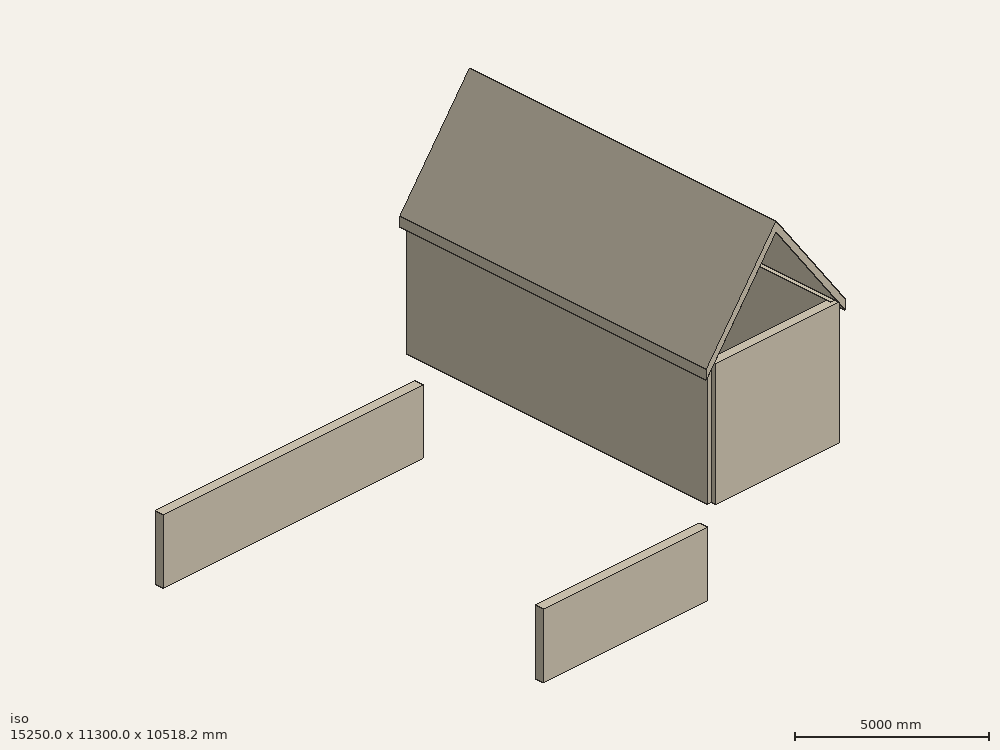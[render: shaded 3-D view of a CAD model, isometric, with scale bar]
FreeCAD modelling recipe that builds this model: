
FCSTD DOCUMENT  (FreeCAD 0.16R6706 (Git))
Label: HorseShoeLane
License: All rights reserved
LicenseURL: http://en.wikipedia.org/wiki/All_rights_reserved
objects: Part::Part2DObjectPython×12, Part::FeaturePython×10, App::DocumentObjectGroup×2, App::DocumentObjectGroupPython×2, Sketcher::SketchObject×1
note: 23 computed .brp shape members not serialized (recipe doc carries the construction recipe); baked Part::Feature solids carry a one-line shape summary decoded from their .brp

FEATURE [Part::Part2DObjectPython] Line  label="External North"  # Draft 2D object (typed FeaturePython)
  ChamferSize = 0
  Closed = false
  End = (4500,0,0)
  FilletRadius = 0
  Length = 4500
  MakeFace = true
  Points = (2) [(0,0,0),(4500,2.75546e-13,0)]
  Start = (0,0,0)
  Subdivisions = 0
FEATURE [Part::Part2DObjectPython] Line001  label="External West"  # Draft 2D object (typed FeaturePython)
  ChamferSize = 0
  Closed = false
  End = (0,-11000,0)
  FilletRadius = 0
  Length = 11000
  MakeFace = true
  Points = (2) [(0,0,0),(0,-11000,0)]
  Start = (0,0,0)
  Subdivisions = 0
FEATURE [Part::Part2DObjectPython] Line002  label="External East N"  # Draft 2D object (typed FeaturePython)
  ChamferSize = 0
  Closed = false
  End = (5600,-5600,0)
  FilletRadius = 0
  Length = 5600
  MakeFace = true
  Points = (2) [(5600,3.42901e-13,0),(5600,-5600,0)]
  Start = (5600,0,0)
  Subdivisions = 0
FEATURE [Part::Part2DObjectPython] Line003  label="External South"  # Draft 2D object (typed FeaturePython)
  ChamferSize = 0
  Closed = false
  End = (4500,-11000,0)
  FilletRadius = 0
  Length = 4500
  MakeFace = true
  Points = (2) [(0,-11000,0),(4500,-11000,0)]
  Start = (0,-11000,0)
  Subdivisions = 0
FEATURE [Part::Part2DObjectPython] Line004  label="External East S"  # Draft 2D object (typed FeaturePython)
  ChamferSize = 0
  Closed = false
  End = (4500,-5600,0)
  FilletRadius = 0
  Length = 5400
  MakeFace = true
  Points = (2) [(4500,-11000,0),(4500,-5600,0)]
  Start = (4500,-11000,0)
  Subdivisions = 0
FEATURE [Part::Part2DObjectPython] Line005  label="External Porch South"  # Draft 2D object (typed FeaturePython)
  ChamferSize = 0
  Closed = false
  End = (5600,-5600,0)
  FilletRadius = 0
  Length = 1100
  MakeFace = true
  Points = (2) [(4500,-5600,0),(5600,-5600,0)]
  Start = (4500,-5600,0)
  Subdivisions = 0
FEATURE [App::DocumentObjectGroup] Group  label="Main Cottage"
  Group = -> [Line,Line001,Line002,Line003,Line004,Line005]
FEATURE [Part::Part2DObjectPython] Line006  label="LF External North"  # Draft 2D object (typed FeaturePython)
  ChamferSize = 0
  Closed = false
  End = (-9500,-300,-3000)
  FilletRadius = 0
  Length = 9500
  MakeFace = true
  Placement = pos=(0,-300,-3000) rot=(0,0,1;0rad)
  Points = (2) [(0,0,0),(-9500,-5.81707e-13,0)]
  Start = (0,-300,-3000)
  Subdivisions = 0
FEATURE [Part::Part2DObjectPython] Line007  label="LF External South"  # Draft 2D object (typed FeaturePython)
  ChamferSize = 0
  Closed = false
  End = (-6000,-10700,-3000)
  FilletRadius = 0
  Length = 6000
  MakeFace = true
  Placement = pos=(0,300,-3000) rot=(0,0,1;0rad)
  Points = (2) [(0,-11000,0),(-6000,-11000,0)]
  Start = (0,-10700,-3000)
  Subdivisions = 0
FEATURE [App::DocumentObjectGroup] Group001  label="Lower Floor"
  Group = -> [Line006,Line007]
FEATURE [Part::FeaturePython] Wall  label="LF South Wall"  # WARN: FeaturePython — macro-defined, semantics opaque (R4)
  Align = 2
  Base = -> Line007
  Face = 0
  Height = 2200
  Length = 6000
  MoveWithHost = false
  Normal = (0,0,0)
  Role = 0
  Width = 300
FEATURE [Part::FeaturePython] Wall001  label="LF North Wall"  # WARN: FeaturePython — macro-defined, semantics opaque (R4)
  Align = 2
  Base = -> Line006
  Face = 0
  Height = 2200
  Length = 9500
  MoveWithHost = false
  Normal = (0,0,0)
  Role = 0
  Width = 300
FEATURE [App::DocumentObjectGroupPython] Floor  label="Lower Floor001"  # scripted group (container) (typed FeaturePython)
  Group = -> [Wall,Wall001]
  Height = 0
FEATURE [Part::Part2DObjectPython] Line008  label="External Porch North"  # Draft 2D object (typed FeaturePython)
  ChamferSize = 0
  Closed = false
  End = (5600,0,0)
  FilletRadius = 0
  Length = 1100
  MakeFace = true
  Placement = pos=(0,5600,0) rot=(0,0,1;0rad)
  Points = (2) [(4500,-5600,0),(5600,-5600,0)]
  Start = (4500,0,0)
  Subdivisions = 0
FEATURE [Part::Part2DObjectPython] Line009  label="MC Internal East"  # Draft 2D object (typed FeaturePython)
  ChamferSize = 0
  Closed = false
  End = (4500,0,0)
  FilletRadius = 0
  Length = 5600
  MakeFace = true
  Points = (2) [(4500,-5600,0),(4500,2.75546e-13,0)]
  Start = (4500,-5600,0)
  Subdivisions = 0
FEATURE [Sketcher::SketchObject] Sketch
  sketch-geometry (3):
    g0: LineSegment StartX=4500 StartY=0 StartZ=0 EndX=5600 EndY=0 EndZ=0
    g1: LineSegment StartX=4500 StartY=-5600 StartZ=0 EndX=5600 EndY=-5600 EndZ=0
    g2: LineSegment StartX=5600 StartY=0 StartZ=0 EndX=5600 EndY=-5600 EndZ=0
FEATURE [Part::FeaturePython] Wall008  label="MC Porch North Wall"  # WARN: FeaturePython — macro-defined, semantics opaque (R4)
  Align = 2
  Base = -> Sketch
  Face = 0
  Height = 2100
  Length = 7800
  MoveWithHost = false
  Normal = (0,0,0)
  Role = 0
  Width = 300
FEATURE [Part::FeaturePython] Wall003  label="MC South Wall"  # WARN: FeaturePython — macro-defined, semantics opaque (R4)
  Align = 2
  Base = -> Line003
  Face = 0
  Height = 4200
  Length = 4500
  MoveWithHost = false
  Normal = (0,0,0)
  Role = 0
  Width = 300
FEATURE [Part::FeaturePython] Wall004  label="MC External West Wall"  # WARN: FeaturePython — macro-defined, semantics opaque (R4)
  Align = 2
  Base = -> Line001
  Face = 0
  Height = 4200
  Length = 11000
  MoveWithHost = false
  Normal = (0,0,0)
  Role = 0
  Width = 300
FEATURE [Part::FeaturePython] Wall006  label="MC External East S Wall"  # WARN: FeaturePython — macro-defined, semantics opaque (R4)
  Align = 2
  Base = -> Line004
  Face = 0
  Height = 4200
  Length = 5400
  MoveWithHost = false
  Normal = (0,0,0)
  Role = 0
  Width = 300
FEATURE [Part::FeaturePython] Wall009  label="Wall"  # WARN: FeaturePython — macro-defined, semantics opaque (R4)
  Align = 2
  Base = -> Line009
  Face = 0
  Height = 4200
  Length = 5600
  MoveWithHost = false
  Normal = (0,0,0)
  Role = 0
  Width = 300
FEATURE [Part::FeaturePython] Wall002  label="MC North Wall"  # WARN: FeaturePython — macro-defined, semantics opaque (R4)
  Align = 2
  Base = -> Line
  Face = 0
  Height = 4200
  Length = 4500
  MoveWithHost = false
  Normal = (0,0,0)
  Role = 0
  Width = 300
FEATURE [App::DocumentObjectGroupPython] Floor001  label="Main Cottage Floor"  # scripted group (container) (typed FeaturePython)
  Group = -> [Line,Line001,Line003,Line002,Line004,Line005,Wall002,Wall003,Wall004,Wall006,Line008,Wall008,Wall009]
  Height = 0
FEATURE [Part::Part2DObjectPython] DWire  # Draft 2D object (typed FeaturePython)
  ChamferSize = 0
  Closed = true
  End = (4500,0,4200)
  FilletRadius = 0
  Length = 31000
  MakeFace = true
  Points = (4) [(0,-8.95295e-15,4200),(-4.54747e-13,-11000,4200),(4500,-11000,4200),(4500,4.33578e-15,4200)]
  Start = (0,0,4200)
  Subdivisions = 0
  Support = -> Wall002
FEATURE [Part::FeaturePython] Roof  # WARN: FeaturePython — macro-defined, semantics opaque (R4)
  Angles = [53,90,53,90]
  Base = -> DWire
  Face = 0
  Heights = [2985.85,2985.85,2985.85,2985.85]
  IdRel = [0,0,0,0]
  MoveWithHost = false
  Overhang = [300,100,300,100]
  Role = 0
  Runs = [2250,0,2250,0]
  Thickness = [200,50,200,50]
FEATURE [Part::Part2DObjectPython] DWire001  # Draft 2D object (typed FeaturePython)
  ChamferSize = 0
  Closed = true
  End = (5600,-5600,2100)
  FilletRadius = 0
  Length = 13400
  MakeFace = true
  Points = (4) [(5600,0,2100),(4500,-6.73556e-14,2100),(4500,-5600,2100),(5600,-5600,2100)]
  Start = (5600,0,2100)
  Subdivisions = 0
  Support = -> Wall008
FEATURE [Part::FeaturePython] Roof001  # WARN: FeaturePython — macro-defined, semantics opaque (R4)
  Angles = [45,45,45,45]
  Base = -> DWire001
  Face = 0
  Heights = [100,100,100,800]
  IdRel = [0,0,0,0]
  MoveWithHost = false
  Overhang = [100,100,100,200]
  Role = 0
  Runs = [100,100,100,800]
  Thickness = [50,50,50,50]
